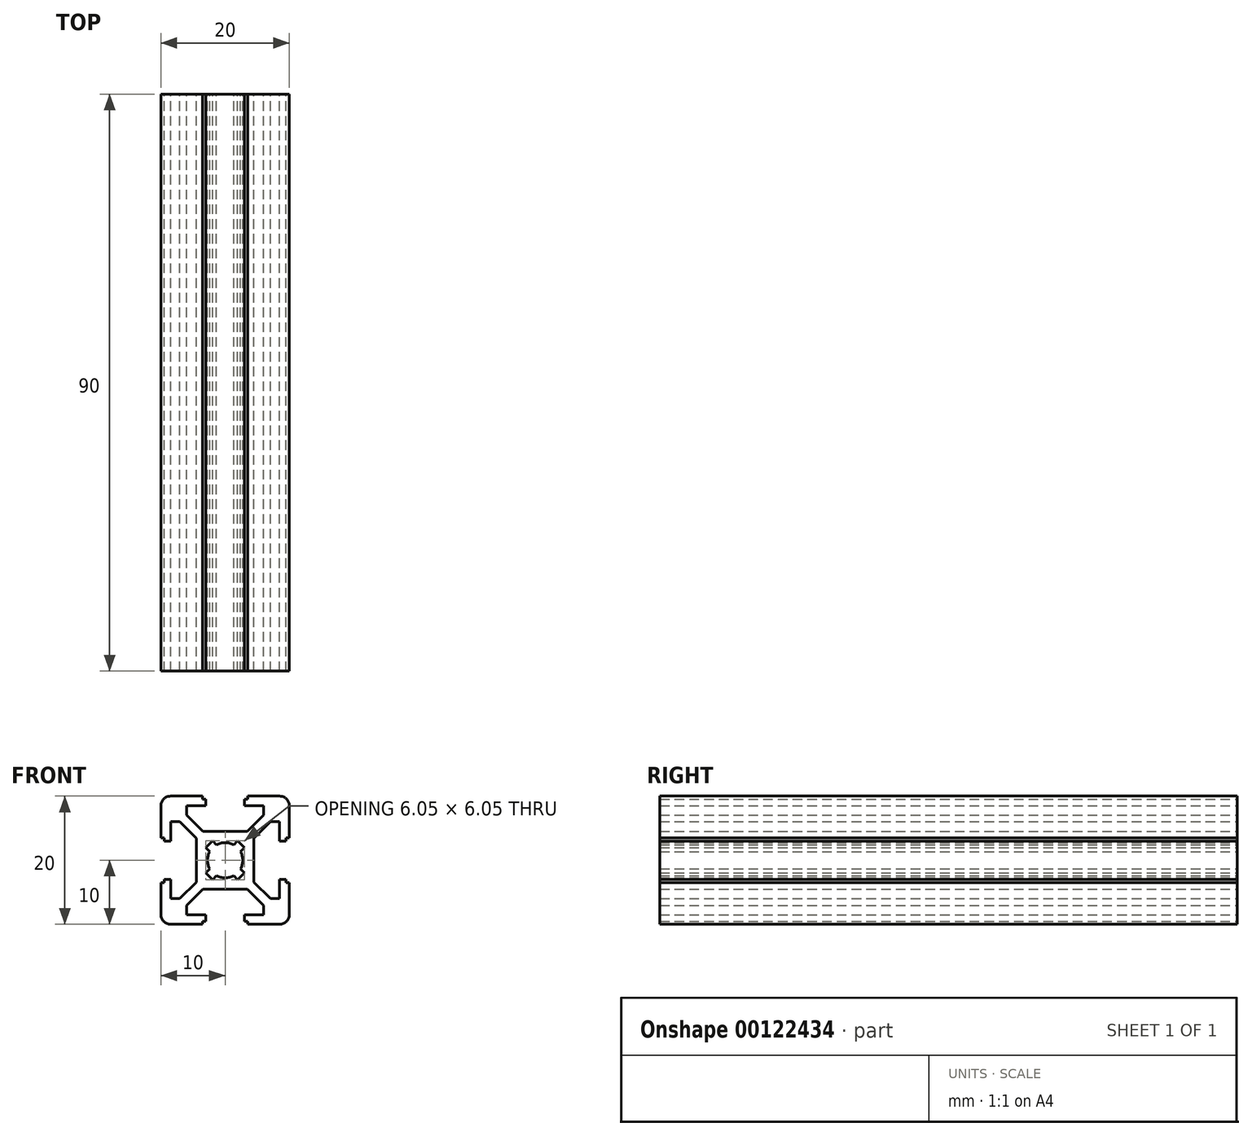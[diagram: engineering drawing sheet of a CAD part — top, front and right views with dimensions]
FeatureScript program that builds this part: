
annotation { "Feature Type Name" : "Feature", "Feature Type Description" : "" }
export const myFeature = defineFeature(function(context is Context, id is Id, definition is map)
    precondition{}
    {
        {
            var Q0;
            Q0=qCreatedBy(makeId("Front.planeOp"),FACE);
            var sketch = newSketch(context, id + "F0", { "sketchPlane" : qUnion([Q0])});
            skLineSegment(sketch, "E0", {"start": v(0, 4.5) * mm, "end": v(3.44, 4.5) * mm});
            skLineSegment(sketch, "E1", {"start": v(3.44, 4.5) * mm, "end": v(6, 7.06) * mm});
            skLineSegment(sketch, "E2", {"start": v(6, 7.06) * mm, "end": v(6, 8.5) * mm});
            skLineSegment(sketch, "E3", {"start": v(6, 8.5) * mm, "end": v(3, 8.5) * mm});
            skLineSegment(sketch, "E4", {"start": v(3, 8.5) * mm, "end": v(3, 9.5) * mm});
            skLineSegment(sketch, "E5", {"start": v(3, 9.5) * mm, "end": v(3.5, 9.5) * mm});
            skLineSegment(sketch, "E6", {"start": v(3.5, 9.5) * mm, "end": v(3.5, 10) * mm});
            skLineSegment(sketch, "E7", {"start": v(3.5, 10) * mm, "end": v(8.5, 10) * mm});
            skLineSegment(sketch, "E8", {"start": v(0, 0) * mm, "end": v(11.95, 11.95) * mm, "construction": true});
            skLineSegment(sketch, "E9.MirrorCS", {"start": v(9.5, 3) * mm, "end": v(9.5, 3.5) * mm});
            skLineSegment(sketch, "E10.MirrorCS", {"start": v(9.5, 3.5) * mm, "end": v(10, 3.5) * mm});
            skLineSegment(sketch, "E11.MirrorCS", {"start": v(4.5, 3.44) * mm, "end": v(7.06, 6) * mm});
            skLineSegment(sketch, "E12.MirrorCS", {"start": v(7.06, 6) * mm, "end": v(8.5, 6) * mm});
            skLineSegment(sketch, "E13.MirrorCS", {"start": v(8.5, 6) * mm, "end": v(8.5, 3) * mm});
            skLineSegment(sketch, "E14.MirrorCS", {"start": v(8.5, 3) * mm, "end": v(9.5, 3) * mm});
            skLineSegment(sketch, "E15.MirrorCS", {"start": v(10, 3.5) * mm, "end": v(10, 8.5) * mm});
            skLineSegment(sketch, "E16.MirrorCS", {"start": v(4.5, 0) * mm, "end": v(4.5, 3.44) * mm});
            skPoint(sketch, "E17.visualSharp", {"position": v(10, 10) * mm});
            skArc(sketch, "E17.filletArc", {"start": v(10, 8.5) * mm, "mid": v(9.56, 9.56) * mm, "end": v(8.5, 10) * mm});
            skArc(sketch, "E18", {"start": v(0, 2.75) * mm, "mid": v(0.7, 2.66) * mm, "end": v(1.34, 2.4) * mm});
            skLineSegment(sketch, "E19", {"start": v(1.34, 2.4) * mm, "end": v(1.96, 3.02) * mm});
            skLineSegment(sketch, "E20", {"start": v(1.96, 3.02) * mm, "end": v(3.02, 1.96) * mm});
            skLineSegment(sketch, "E21", {"start": v(3.02, 1.96) * mm, "end": v(2.4, 1.34) * mm});
            skArc(sketch, "E22.trimOffspring", {"start": v(2.4, 1.34) * mm, "mid": v(2.66, 0.7) * mm, "end": v(2.75, 0) * mm});
            skLineSegment(sketch, "E23.MirrorCS", {"start": v(1.96, 3.02) * mm, "end": v(1.34, 2.4) * mm});
            skLineSegment(sketch, "E24.MirrorCS", {"start": v(2.4, 1.34) * mm, "end": v(3.02, 1.96) * mm});
            skArc(sketch, "E25.MirrorCS", {"start": v(8.5, 10) * mm, "mid": v(9.56, 9.56) * mm, "end": v(10, 8.5) * mm});
            skArc(sketch, "E26.MirrorCS", {"start": v(2.75, 0) * mm, "mid": v(2.66, 0.7) * mm, "end": v(2.4, 1.34) * mm});
            skArc(sketch, "E27.MirrorCS", {"start": v(1.34, 2.4) * mm, "mid": v(0.7, 2.66) * mm, "end": v(0, 2.75) * mm});
            skLineSegment(sketch, "E28.MirrorCS", {"start": v(3.02, 1.96) * mm, "end": v(1.96, 3.02) * mm});
            skLineSegment(sketch, "E29.MirrorCS", {"start": v(3, -9.5) * mm, "end": v(3.5, -9.5) * mm});
            skLineSegment(sketch, "E30.MirrorCS", {"start": v(9.5, -3) * mm, "end": v(9.5, -3.5) * mm});
            skLineSegment(sketch, "E31.MirrorCS", {"start": v(9.5, -3.5) * mm, "end": v(10, -3.5) * mm});
            skLineSegment(sketch, "E32.MirrorCS", {"start": v(3.5, -9.5) * mm, "end": v(3.5, -10) * mm});
            skLineSegment(sketch, "E33.MirrorCS", {"start": v(6, -7.06) * mm, "end": v(6, -8.5) * mm});
            skArc(sketch, "E34.MirrorCS", {"start": v(8.5, -10) * mm, "mid": v(9.56, -9.56) * mm, "end": v(10, -8.5) * mm});
            skLineSegment(sketch, "E35.MirrorCS", {"start": v(3.5, -10) * mm, "end": v(8.5, -10) * mm});
            skLineSegment(sketch, "E36.MirrorCS", {"start": v(0, -4.5) * mm, "end": v(3.44, -4.5) * mm});
            skLineSegment(sketch, "E37.MirrorCS", {"start": v(3.02, -1.96) * mm, "end": v(1.96, -3.02) * mm});
            skLineSegment(sketch, "E38.MirrorCS", {"start": v(1.34, -2.4) * mm, "end": v(1.96, -3.02) * mm});
            skLineSegment(sketch, "E39.MirrorCS", {"start": v(4.5, -3.44) * mm, "end": v(7.06, -6) * mm});
            skLineSegment(sketch, "E40.MirrorCS", {"start": v(7.06, -6) * mm, "end": v(8.5, -6) * mm});
            skLineSegment(sketch, "E41.MirrorCS", {"start": v(3.44, -4.5) * mm, "end": v(6, -7.06) * mm});
            skLineSegment(sketch, "E42.MirrorCS", {"start": v(6, -8.5) * mm, "end": v(3, -8.5) * mm});
            skLineSegment(sketch, "E43.MirrorCS", {"start": v(8.5, -6) * mm, "end": v(8.5, -3) * mm});
            skLineSegment(sketch, "E44.MirrorCS", {"start": v(10, -3.5) * mm, "end": v(10, -8.5) * mm});
            skLineSegment(sketch, "E45.MirrorCS", {"start": v(8.5, -3) * mm, "end": v(9.5, -3) * mm});
            skLineSegment(sketch, "E46.MirrorCS", {"start": v(3.02, -1.96) * mm, "end": v(2.4, -1.34) * mm});
            skLineSegment(sketch, "E47.MirrorCS", {"start": v(4.5, 0) * mm, "end": v(4.5, -3.44) * mm});
            skLineSegment(sketch, "E48.MirrorCS", {"start": v(3, -8.5) * mm, "end": v(3, -9.5) * mm});
            skPoint(sketch, "E49.MirrorP", {"position": v(10, -10) * mm});
            skLineSegment(sketch, "E50.MirrorCS", {"start": v(1.96, -3.02) * mm, "end": v(3.02, -1.96) * mm});
            skLineSegment(sketch, "E51.MirrorCS", {"start": v(1.96, -3.02) * mm, "end": v(1.34, -2.4) * mm});
            skArc(sketch, "E52.MirrorCS", {"start": v(10, -8.5) * mm, "mid": v(9.56, -9.56) * mm, "end": v(8.5, -10) * mm});
            skArc(sketch, "E53.MirrorCS", {"start": v(0, -2.75) * mm, "mid": v(0.7, -2.66) * mm, "end": v(1.34, -2.4) * mm});
            skArc(sketch, "E54.MirrorCS", {"start": v(2.75, 0) * mm, "mid": v(2.66, -0.7) * mm, "end": v(2.4, -1.34) * mm});
            skArc(sketch, "E55.MirrorCS", {"start": v(2.4, -1.34) * mm, "mid": v(2.66, -0.7) * mm, "end": v(2.75, 0) * mm});
            skLineSegment(sketch, "E56.MirrorCS", {"start": v(2.4, -1.34) * mm, "end": v(3.02, -1.96) * mm});
            skArc(sketch, "E57.MirrorCS", {"start": v(1.34, -2.4) * mm, "mid": v(0.7, -2.66) * mm, "end": v(0, -2.75) * mm});
            skLineSegment(sketch, "E58.MirrorCS", {"start": v(-1.34, 2.4) * mm, "end": v(-1.96, 3.02) * mm});
            skLineSegment(sketch, "E59.MirrorCS", {"start": v(-9.5, 3) * mm, "end": v(-9.5, 3.5) * mm});
            skLineSegment(sketch, "E60.MirrorCS", {"start": v(-9.5, -3) * mm, "end": v(-9.5, -3.5) * mm});
            skLineSegment(sketch, "E61.MirrorCS", {"start": v(-3.02, 1.96) * mm, "end": v(-2.4, 1.34) * mm});
            skLineSegment(sketch, "E62.MirrorCS", {"start": v(-3.5, 9.5) * mm, "end": v(-3.5, 10) * mm});
            skLineSegment(sketch, "E63.MirrorCS", {"start": v(-3, -9.5) * mm, "end": v(-3.5, -9.5) * mm});
            skLineSegment(sketch, "E64.MirrorCS", {"start": v(-1.34, -2.4) * mm, "end": v(-1.96, -3.02) * mm});
            skLineSegment(sketch, "E65.MirrorCS", {"start": v(-3, 9.5) * mm, "end": v(-3.5, 9.5) * mm});
            skLineSegment(sketch, "E66.MirrorCS", {"start": v(-9.5, -3.5) * mm, "end": v(-10, -3.5) * mm});
            skLineSegment(sketch, "E67.MirrorCS", {"start": v(-9.5, 3.5) * mm, "end": v(-10, 3.5) * mm});
            skLineSegment(sketch, "E68.MirrorCS", {"start": v(-3.02, -1.96) * mm, "end": v(-2.4, -1.34) * mm});
            skLineSegment(sketch, "E69.MirrorCS", {"start": v(-3.5, -9.5) * mm, "end": v(-3.5, -10) * mm});
            skLineSegment(sketch, "E70.MirrorCS", {"start": v(-1.96, -3.02) * mm, "end": v(-1.34, -2.4) * mm});
            skLineSegment(sketch, "E71.MirrorCS", {"start": v(-2.4, -1.34) * mm, "end": v(-3.02, -1.96) * mm});
            skLineSegment(sketch, "E72.MirrorCS", {"start": v(-1.96, 3.02) * mm, "end": v(-1.34, 2.4) * mm});
            skLineSegment(sketch, "E73.MirrorCS", {"start": v(-2.4, 1.34) * mm, "end": v(-3.02, 1.96) * mm});
            skLineSegment(sketch, "E74.MirrorCS", {"start": v(-3.5, 10) * mm, "end": v(-8.5, 10) * mm});
            skLineSegment(sketch, "E75.MirrorCS", {"start": v(-8.5, 6) * mm, "end": v(-8.5, 3) * mm});
            skLineSegment(sketch, "E76.MirrorCS", {"start": v(-6, 8.5) * mm, "end": v(-3, 8.5) * mm});
            skLineSegment(sketch, "E77.MirrorCS", {"start": v(-3, 8.5) * mm, "end": v(-3, 9.5) * mm});
            skLineSegment(sketch, "E78.MirrorCS", {"start": v(-3.5, -10) * mm, "end": v(-8.5, -10) * mm});
            skLineSegment(sketch, "E79.MirrorCS", {"start": v(-6, 7.06) * mm, "end": v(-6, 8.5) * mm});
            skLineSegment(sketch, "E80.MirrorCS", {"start": v(-3, -8.5) * mm, "end": v(-3, -9.5) * mm});
            skPoint(sketch, "E81.MirrorP", {"position": v(-10, -10) * mm});
            skLineSegment(sketch, "E82.MirrorCS", {"start": v(-4.5, 3.44) * mm, "end": v(-7.06, 6) * mm});
            skLineSegment(sketch, "E83.MirrorCS", {"start": v(-7.06, 6) * mm, "end": v(-8.5, 6) * mm});
            skLineSegment(sketch, "E84.MirrorCS", {"start": v(-3.44, 4.5) * mm, "end": v(-6, 7.06) * mm});
            skLineSegment(sketch, "E85.MirrorCS", {"start": v(-10, -3.5) * mm, "end": v(-10, -8.5) * mm});
            skLineSegment(sketch, "E86.MirrorCS", {"start": v(-7.06, -6) * mm, "end": v(-8.5, -6) * mm});
            skLineSegment(sketch, "E87.MirrorCS", {"start": v(-8.5, -6) * mm, "end": v(-8.5, -3) * mm});
            skLineSegment(sketch, "E88.MirrorCS", {"start": v(-4.5, 0) * mm, "end": v(-4.5, -3.44) * mm});
            skLineSegment(sketch, "E89.MirrorCS", {"start": v(-4.5, -3.44) * mm, "end": v(-7.06, -6) * mm});
            skLineSegment(sketch, "E90.MirrorCS", {"start": v(-1.96, 3.02) * mm, "end": v(-3.02, 1.96) * mm});
            skLineSegment(sketch, "E91.MirrorCS", {"start": v(-4.5, 0) * mm, "end": v(-4.5, 3.44) * mm});
            skLineSegment(sketch, "E92.MirrorCS", {"start": v(0, -4.5) * mm, "end": v(-3.44, -4.5) * mm});
            skLineSegment(sketch, "E93.MirrorCS", {"start": v(-6, -7.06) * mm, "end": v(-6, -8.5) * mm});
            skArc(sketch, "E94.MirrorCS", {"start": v(-8.5, 10) * mm, "mid": v(-9.56, 9.56) * mm, "end": v(-10, 8.5) * mm});
            skLineSegment(sketch, "E95.MirrorCS", {"start": v(-10, 3.5) * mm, "end": v(-10, 8.5) * mm});
            skPoint(sketch, "E96.MirrorP", {"position": v(-10, 10) * mm});
            skLineSegment(sketch, "E97.MirrorCS", {"start": v(-6, -8.5) * mm, "end": v(-3, -8.5) * mm});
            skArc(sketch, "E98.MirrorCS", {"start": v(-8.5, -10) * mm, "mid": v(-9.56, -9.56) * mm, "end": v(-10, -8.5) * mm});
            skLineSegment(sketch, "E99.MirrorCS", {"start": v(0, 4.5) * mm, "end": v(-3.44, 4.5) * mm});
            skLineSegment(sketch, "E100.MirrorCS", {"start": v(-8.5, 3) * mm, "end": v(-9.5, 3) * mm});
            skLineSegment(sketch, "E101.MirrorCS", {"start": v(-1.96, -3.02) * mm, "end": v(-3.02, -1.96) * mm});
            skLineSegment(sketch, "E102.MirrorCS", {"start": v(-8.5, -3) * mm, "end": v(-9.5, -3) * mm});
            skLineSegment(sketch, "E103.MirrorCS", {"start": v(-3.44, -4.5) * mm, "end": v(-6, -7.06) * mm});
            skLineSegment(sketch, "E104.MirrorCS", {"start": v(-3.02, -1.96) * mm, "end": v(-1.96, -3.02) * mm});
            skArc(sketch, "E105.MirrorCS", {"start": v(-10, 8.5) * mm, "mid": v(-9.56, 9.56) * mm, "end": v(-8.5, 10) * mm});
            skArc(sketch, "E106.MirrorCS", {"start": v(-10, -8.5) * mm, "mid": v(-9.56, -9.56) * mm, "end": v(-8.5, -10) * mm});
            skLineSegment(sketch, "E107.MirrorCS", {"start": v(-3.02, 1.96) * mm, "end": v(-1.96, 3.02) * mm});
            skArc(sketch, "E108.MirrorCS", {"start": v(0, -2.75) * mm, "mid": v(-0.7, -2.66) * mm, "end": v(-1.34, -2.4) * mm});
            skArc(sketch, "E109.MirrorCS", {"start": v(-1.34, -2.4) * mm, "mid": v(-0.7, -2.66) * mm, "end": v(0, -2.75) * mm});
            skArc(sketch, "E110.MirrorCS", {"start": v(0, 2.75) * mm, "mid": v(-0.7, 2.66) * mm, "end": v(-1.34, 2.4) * mm});
            skArc(sketch, "E111.MirrorCS", {"start": v(-2.75, 0) * mm, "mid": v(-2.66, -0.7) * mm, "end": v(-2.4, -1.34) * mm});
            skArc(sketch, "E112.MirrorCS", {"start": v(-2.75, 0) * mm, "mid": v(-2.66, 0.7) * mm, "end": v(-2.4, 1.34) * mm});
            skArc(sketch, "E113.MirrorCS", {"start": v(-2.4, 1.34) * mm, "mid": v(-2.66, 0.7) * mm, "end": v(-2.75, 0) * mm});
            skArc(sketch, "E114.MirrorCS", {"start": v(-1.34, 2.4) * mm, "mid": v(-0.7, 2.66) * mm, "end": v(0, 2.75) * mm});
            skArc(sketch, "E115.MirrorCS", {"start": v(-2.4, -1.34) * mm, "mid": v(-2.66, -0.7) * mm, "end": v(-2.75, 0) * mm});
            skSolve(sketch);
        }
        {
            var Q0;
            Q0 = qSketchRegion(id + "F0", true);
            extrude(context, id + "F1", {"entities" : qUnion([Q0]), "depth" : 90 * mm});
        }
    });
